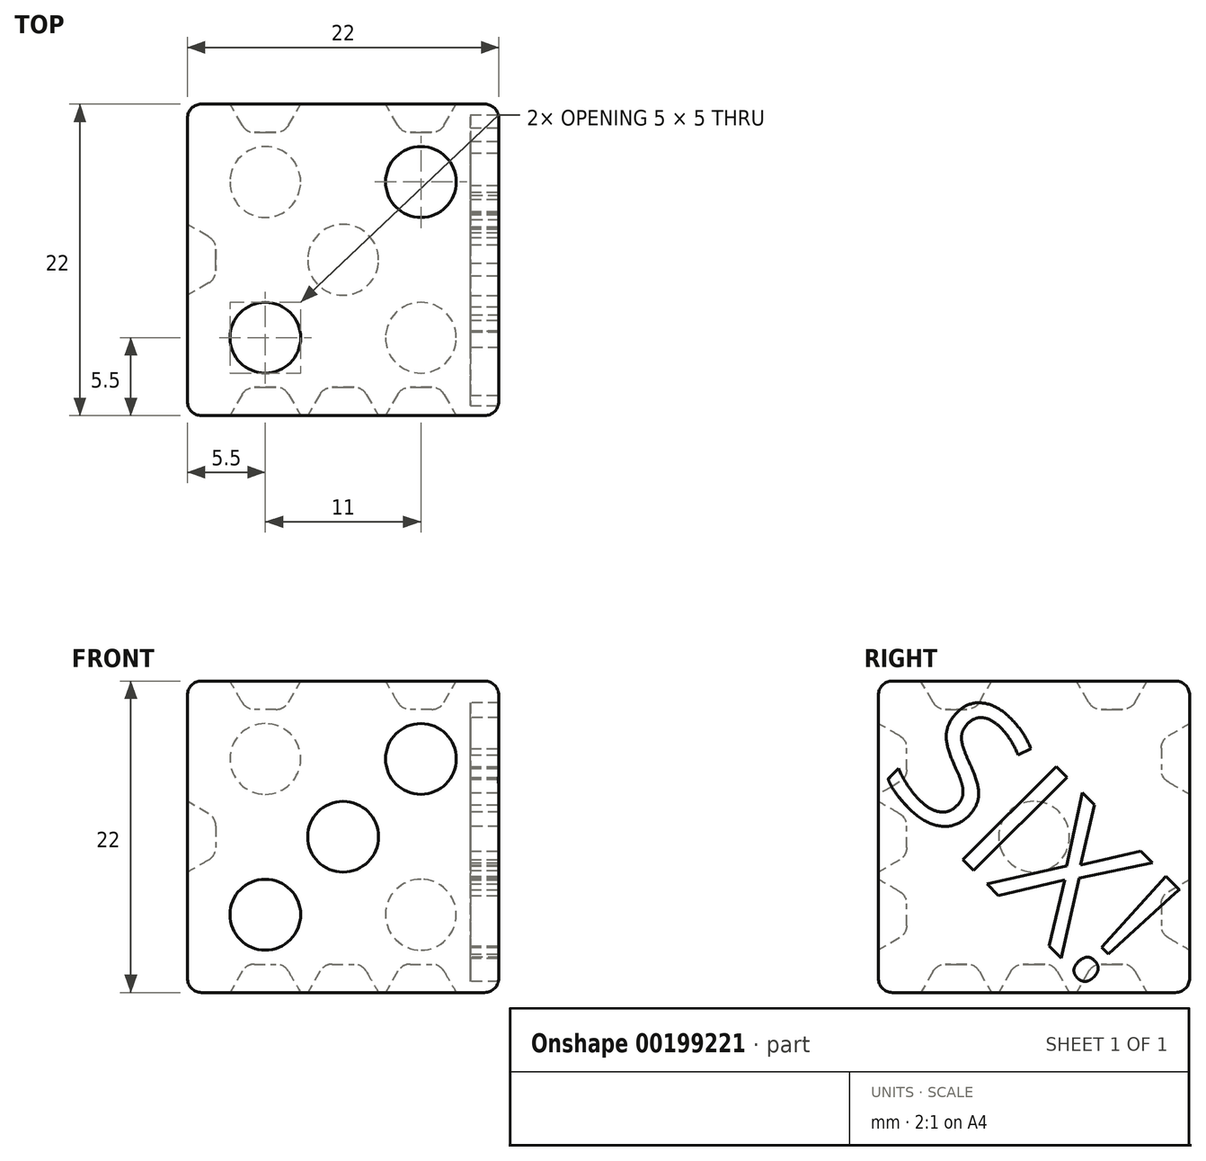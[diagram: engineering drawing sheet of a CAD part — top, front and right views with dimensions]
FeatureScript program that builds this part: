
annotation { "Feature Type Name" : "Feature", "Feature Type Description" : "" }
export const myFeature = defineFeature(function(context is Context, id is Id, definition is map)
    precondition{}
    {
        {
            var Q0;
            Q0=qCreatedBy(makeId("Top.planeOp"),FACE);
            var sketch = newSketch(context, id + "F0", { "sketchPlane" : qUnion([Q0])});
            skLineSegment(sketch, "E0.bottom", {"start": v(11, 11) * mm, "end": v(-11, 11) * mm});
            skLineSegment(sketch, "E0.top", {"start": v(11, -11) * mm, "end": v(-11, -11) * mm});
            skLineSegment(sketch, "E0.left", {"start": v(11, 11) * mm, "end": v(11, -11) * mm});
            skLineSegment(sketch, "E0.right", {"start": v(-11, 11) * mm, "end": v(-11, -11) * mm});
            skPoint(sketch, "E0.middle", {"position": v(0, 0) * mm});
            skSolve(sketch);
        }
        {
            var Q0;
            Q0=makeQuery(id+"F0.imprint","IMPRINT",FACE,{"disambiguationData":[TD([[makeQuery(id+"F0.imprint","IMPRINT",EDGE,{"derivedFrom":sQuery(id+"F0.wireOp",EDGE,"E0.bottom")}),1.0]])]});
            extrude(context, id + "F1", {"entities" : qUnion([Q0]), "depth" : 22 * mm});
        }
        {
            var Q0;
            Q0=makeQuery(id+"F1.opExtrude","SWEPT_FACE",FACE,{"disambiguationData":[OSD([sQuery(id+"F0.wireOp",EDGE,"E0.right")])]});
            var sketch = newSketch(context, id + "F2", { "sketchPlane" : qUnion([Q0])});
            skLineSegment(sketch, "E1", {"start": v(0, 22) * mm, "end": v(0, 0) * mm, "construction": true});
            skCircle(sketch, "E2", {"center": v(0, 11) * mm, "radius": 2.5 * mm});
            skSolve(sketch);
        }
        {
            var Q0;
            Q0 = qSketchRegion(id + "F2", true);
            extrude(context, id + "F3", {"entities" : qUnion([Q0]), "operationType" : NewBodyOperationType.REMOVE, "oppositeDirection" : true, "depth" : 2 * mm, "hasDraft" : true, "draftAngle" : 30 * degree, "draftPullDirection" : true});
        }
        {
            var Q0;
            Q0=makeQuery(id+"F1.opExtrude","CAP_FACE",FACE,{"disambiguationData":[OSD([sQuery(id+"F0.wireOp",EDGE,"E0.bottom"),sQuery(id+"F0.wireOp",EDGE,"E0.top"),sQuery(id+"F0.wireOp",EDGE,"E0.left"),sQuery(id+"F0.wireOp",EDGE,"E0.right")])],"isStart":false});
            var sketch = newSketch(context, id + "F4", { "sketchPlane" : qUnion([Q0])});
            skLineSegment(sketch, "E3", {"start": v(11, 11) * mm, "end": v(-11, -11) * mm, "construction": true});
            skLineSegment(sketch, "E4", {"start": v(11, 11) * mm, "end": v(11, 0) * mm, "construction": true});
            skLineSegment(sketch, "E5", {"start": v(11, 0) * mm, "end": v(-11, 0) * mm, "construction": true});
            skLineSegment(sketch, "E6", {"start": v(-11, 0) * mm, "end": v(-11, -11) * mm, "construction": true});
            skLineSegment(sketch, "E7", {"start": v(-11, -5.5) * mm, "end": v(11, -5.5) * mm, "construction": true});
            skLineSegment(sketch, "E8", {"start": v(11, 5.5) * mm, "end": v(-11, 5.5) * mm, "construction": true});
            skCircle(sketch, "E9", {"center": v(5.5, 5.5) * mm, "radius": 2.5 * mm});
            skCircle(sketch, "E10", {"center": v(-5.5, -5.5) * mm, "radius": 2.5 * mm});
            skSolve(sketch);
        }
        {
            var Q0;
            Q0 = qSketchRegion(id + "F4", true);
            extrude(context, id + "F5", {"entities" : qUnion([Q0]), "operationType" : NewBodyOperationType.REMOVE, "oppositeDirection" : true, "depth" : 2 * mm, "hasDraft" : true, "draftAngle" : 30 * degree, "draftPullDirection" : true});
        }
        {
            var Q0;
            Q0=makeQuery(id+"F1.opExtrude","SWEPT_FACE",FACE,{"disambiguationData":[OSD([sQuery(id+"F0.wireOp",EDGE,"E0.top")])]});
            var sketch = newSketch(context, id + "F6", { "sketchPlane" : qUnion([Q0])});
            skLineSegment(sketch, "E11", {"start": v(11, 11) * mm, "end": v(-11, 11) * mm, "construction": true});
            skLineSegment(sketch, "E12", {"start": v(11, 22) * mm, "end": v(0, 11) * mm, "construction": true});
            skLineSegment(sketch, "E13", {"start": v(0, 11) * mm, "end": v(-11, 0) * mm, "construction": true});
            skCircle(sketch, "E14", {"center": v(5.5, 16.5) * mm, "radius": 2.5 * mm});
            skCircle(sketch, "E15", {"center": v(0, 11) * mm, "radius": 2.5 * mm});
            skCircle(sketch, "E16", {"center": v(-5.5, 5.5) * mm, "radius": 2.5 * mm});
            skSolve(sketch);
        }
        {
            var Q0;
            Q0 = qSketchRegion(id + "F6", true);
            extrude(context, id + "F7", {"entities" : qUnion([Q0]), "operationType" : NewBodyOperationType.REMOVE, "oppositeDirection" : true, "depth" : 2 * mm, "hasDraft" : true, "draftAngle" : 30 * degree, "draftPullDirection" : true});
        }
        {
            var Q0;
            Q0=makeQuery(id+"F1.opExtrude","SWEPT_FACE",FACE,{"disambiguationData":[OSD([sQuery(id+"F0.wireOp",EDGE,"E0.bottom")])]});
            var sketch = newSketch(context, id + "F8", { "sketchPlane" : qUnion([Q0])});
            skLineSegment(sketch, "E17", {"start": v(-11, 22) * mm, "end": v(11, 22) * mm, "construction": true});
            skLineSegment(sketch, "E18", {"start": v(0, 22) * mm, "end": v(0, 11) * mm, "construction": true});
            skPoint(sketch, "E18.endSnap0", {"position": v(-11, 11) * mm});
            skLineSegment(sketch, "E19", {"start": v(0, 11) * mm, "end": v(0, 0) * mm, "construction": true});
            skLineSegment(sketch, "E20", {"start": v(0, 11) * mm, "end": v(11, 11) * mm, "construction": true});
            skLineSegment(sketch, "E21", {"start": v(0, 22) * mm, "end": v(11, 11) * mm, "construction": true});
            skCircle(sketch, "E22", {"center": v(5.5, 16.5) * mm, "radius": 2.5 * mm});
            skCircle(sketch, "E23.MirrorC", {"center": v(-5.5, 16.5) * mm, "radius": 2.5 * mm});
            skCircle(sketch, "E24.MirrorC", {"center": v(5.5, 5.5) * mm, "radius": 2.5 * mm});
            skCircle(sketch, "E25.MirrorC", {"center": v(-5.5, 5.5) * mm, "radius": 2.5 * mm});
            skSolve(sketch);
        }
        {
            var Q0;
            Q0 = qSketchRegion(id + "F8", true);
            extrude(context, id + "F9", {"entities" : qUnion([Q0]), "operationType" : NewBodyOperationType.REMOVE, "oppositeDirection" : true, "depth" : 2 * mm, "hasDraft" : true, "draftAngle" : 30 * degree, "draftPullDirection" : true});
        }
        {
            var Q0;
            Q0=makeQuery(id+"F1.opExtrude","CAP_FACE",FACE,{"disambiguationData":[OSD([sQuery(id+"F0.wireOp",EDGE,"E0.bottom"),sQuery(id+"F0.wireOp",EDGE,"E0.top"),sQuery(id+"F0.wireOp",EDGE,"E0.left"),sQuery(id+"F0.wireOp",EDGE,"E0.right")])],"isStart":true});
            var sketch = newSketch(context, id + "F10", { "sketchPlane" : qUnion([Q0])});
            skLineSegment(sketch, "E26", {"start": v(11, -11) * mm, "end": v(0, 0) * mm, "construction": true});
            skLineSegment(sketch, "E27", {"start": v(0, 0) * mm, "end": v(-11, 11) * mm, "construction": true});
            skLineSegment(sketch, "E28", {"start": v(11, 0) * mm, "end": v(-11, 0) * mm, "construction": true});
            skCircle(sketch, "E29", {"center": v(0, 0) * mm, "radius": 2.5 * mm});
            skCircle(sketch, "E30", {"center": v(5.5, -5.5) * mm, "radius": 2.5 * mm});
            skCircle(sketch, "E31", {"center": v(-5.5, 5.5) * mm, "radius": 2.5 * mm});
            skLineSegment(sketch, "E32", {"start": v(0, 0) * mm, "end": v(-11, -11) * mm, "construction": true});
            skLineSegment(sketch, "E33", {"start": v(0, 0) * mm, "end": v(11, 11) * mm, "construction": true});
            skCircle(sketch, "E34", {"center": v(5.5, 5.5) * mm, "radius": 2.5 * mm});
            skCircle(sketch, "E35", {"center": v(-5.5, -5.5) * mm, "radius": 2.5 * mm});
            skSolve(sketch);
        }
        {
            var Q0;
            Q0 = qSketchRegion(id + "F10", true);
            extrude(context, id + "F11", {"entities" : qUnion([Q0]), "operationType" : NewBodyOperationType.REMOVE, "oppositeDirection" : true, "depth" : 2 * mm, "hasDraft" : true, "draftAngle" : 30 * degree, "draftPullDirection" : true});
        }
        {
            var Q0;
            Q0=makeQuery(id+"F1.opExtrude","SWEPT_FACE",FACE,{"disambiguationData":[OSD([sQuery(id+"F0.wireOp",EDGE,"E0.left")])]});
            var sketch = newSketch(context, id + "F12", { "sketchPlane" : qUnion([Q0])});
            skText(sketch, "E36", { "text": "SIX!", "fontName": "OpenSans-Regular.ttf"});
            skLineSegment(sketch, "E37", {"start": v(11, 0) * mm, "end": v(-11, 22) * mm, "construction": true});
            skLineSegment(sketch, "E38", {"start": v(-11, 0) * mm, "end": v(0, 11) * mm, "construction": true});
            skPoint(sketch, "E38.endSnap0", {"position": v(0, 11) * mm});
            const initialGuessF12  = {"E36": [-0.011, 0.01535, 0.7071, -0.7071, 0.0094]};
            skSetInitialGuess(sketch, initialGuessF12);
            skSolve(sketch);
        }
        {
            var Q0;
            Q0 = qSketchRegion(id + "F12", true);
            extrude(context, id + "F13", {"entities" : qUnion([Q0]), "operationType" : NewBodyOperationType.REMOVE, "oppositeDirection" : true, "depth" : 2 * mm});
        }
        {
            var Q0;
            Q0=makeQuery(id+"F1.opExtrude","SWEPT_EDGE",EDGE,{"disambiguationData":[OSD([sQuery(id+"F0.wireOp",EDGE,"E0.top"),sQuery(id+"F0.wireOp",EDGE,"E0.left")])]});
            var Q1;
            Q1=makeQuery(id+"F1.opExtrude","CAP_EDGE",EDGE,{"disambiguationData":[OSD([sQuery(id+"F0.wireOp",EDGE,"E0.left")])],"isStart":true});
            var Q2;
            Q2=makeQuery(id+"F1.opExtrude","SWEPT_EDGE",EDGE,{"disambiguationData":[OSD([sQuery(id+"F0.wireOp",EDGE,"E0.bottom"),sQuery(id+"F0.wireOp",EDGE,"E0.left")])]});
            var Q3;
            Q3=makeQuery(id+"F1.opExtrude","CAP_EDGE",EDGE,{"disambiguationData":[OSD([sQuery(id+"F0.wireOp",EDGE,"E0.left")])],"isStart":false});
            var Q4;
            Q4=makeQuery(id+"F1.opExtrude","SWEPT_EDGE",EDGE,{"disambiguationData":[OSD([sQuery(id+"F0.wireOp",EDGE,"E0.top"),sQuery(id+"F0.wireOp",EDGE,"E0.right")])]});
            var Q5;
            Q5=makeQuery(id+"F1.opExtrude","CAP_EDGE",EDGE,{"disambiguationData":[OSD([sQuery(id+"F0.wireOp",EDGE,"E0.right")])],"isStart":true});
            var Q6;
            Q6=makeQuery(id+"F1.opExtrude","CAP_EDGE",EDGE,{"disambiguationData":[OSD([sQuery(id+"F0.wireOp",EDGE,"E0.top")])],"isStart":true});
            var Q7;
            Q7=makeQuery(id+"F1.opExtrude","CAP_EDGE",EDGE,{"disambiguationData":[OSD([sQuery(id+"F0.wireOp",EDGE,"E0.bottom")])],"isStart":true});
            var Q8;
            Q8=makeQuery(id+"F1.opExtrude","CAP_EDGE",EDGE,{"disambiguationData":[OSD([sQuery(id+"F0.wireOp",EDGE,"E0.top")])],"isStart":false});
            var Q9;
            Q9=makeQuery(id+"F1.opExtrude","SWEPT_EDGE",EDGE,{"disambiguationData":[OSD([sQuery(id+"F0.wireOp",EDGE,"E0.bottom"),sQuery(id+"F0.wireOp",EDGE,"E0.right")])]});
            var Q10;
            Q10=makeQuery(id+"F1.opExtrude","CAP_EDGE",EDGE,{"disambiguationData":[OSD([sQuery(id+"F0.wireOp",EDGE,"E0.bottom")])],"isStart":false});
            var Q11;
            Q11=makeQuery(id+"F1.opExtrude","CAP_EDGE",EDGE,{"disambiguationData":[OSD([sQuery(id+"F0.wireOp",EDGE,"E0.right")])],"isStart":false});
            var Q12;
            Q12=makeQuery(id+"F9.boolean.opBoolean","COPY",EDGE,{"derivedFrom":makeQuery(id+"F9.opExtrude","CAP_EDGE",EDGE,{"disambiguationData":[OSD([sQuery(id+"F8.wireOp",EDGE,"E22")])],"isStart":false})});
            var Q13;
            Q13=makeQuery(id+"F9.boolean.opBoolean","COPY",EDGE,{"derivedFrom":makeQuery(id+"F9.opExtrude","CAP_EDGE",EDGE,{"disambiguationData":[OSD([sQuery(id+"F8.wireOp",EDGE,"E24.MirrorC")])],"isStart":false})});
            var Q14;
            Q14=makeQuery(id+"F9.boolean.opBoolean","COPY",EDGE,{"derivedFrom":makeQuery(id+"F9.opExtrude","CAP_EDGE",EDGE,{"disambiguationData":[OSD([sQuery(id+"F8.wireOp",EDGE,"E25.MirrorC")])],"isStart":false})});
            var Q15;
            Q15=makeQuery(id+"F9.boolean.opBoolean","COPY",EDGE,{"derivedFrom":makeQuery(id+"F9.opExtrude","CAP_EDGE",EDGE,{"disambiguationData":[OSD([sQuery(id+"F8.wireOp",EDGE,"E23.MirrorC")])],"isStart":false})});
            var Q16;
            Q16=makeQuery(id+"F5.boolean.opBoolean","COPY",FACE,{"derivedFrom":makeQuery(id+"F5.opExtrude","CAP_FACE",FACE,{"disambiguationData":[OSD([sQuery(id+"F4.wireOp",EDGE,"E9")])],"isStart":false})});
            var Q17;
            Q17=makeQuery(id+"F5.boolean.opBoolean","COPY",EDGE,{"derivedFrom":makeQuery(id+"F5.opExtrude","CAP_EDGE",EDGE,{"disambiguationData":[OSD([sQuery(id+"F4.wireOp",EDGE,"E10")])],"isStart":false})});
            var Q18;
            Q18=makeQuery(id+"F11.boolean.opBoolean","COPY",FACE,{"derivedFrom":makeQuery(id+"F11.opExtrude","CAP_FACE",FACE,{"disambiguationData":[OSD([sQuery(id+"F10.wireOp",EDGE,"E35")])],"isStart":false})});
            var Q19;
            Q19=makeQuery(id+"F11.boolean.opBoolean","COPY",FACE,{"derivedFrom":makeQuery(id+"F11.opExtrude","CAP_FACE",FACE,{"disambiguationData":[OSD([sQuery(id+"F10.wireOp",EDGE,"E30")])],"isStart":false})});
            var Q20;
            Q20=makeQuery(id+"F11.boolean.opBoolean","COPY",FACE,{"derivedFrom":makeQuery(id+"F11.opExtrude","CAP_FACE",FACE,{"disambiguationData":[OSD([sQuery(id+"F10.wireOp",EDGE,"E29")])],"isStart":false})});
            var Q21;
            Q21=makeQuery(id+"F11.boolean.opBoolean","COPY",FACE,{"derivedFrom":makeQuery(id+"F11.opExtrude","CAP_FACE",FACE,{"disambiguationData":[OSD([sQuery(id+"F10.wireOp",EDGE,"E34")])],"isStart":false})});
            var Q22;
            Q22=makeQuery(id+"F11.boolean.opBoolean","COPY",FACE,{"derivedFrom":makeQuery(id+"F11.opExtrude","CAP_FACE",FACE,{"disambiguationData":[OSD([sQuery(id+"F10.wireOp",EDGE,"E31")])],"isStart":false})});
            var Q23;
            Q23=makeQuery(id+"F7.boolean.opBoolean","COPY",FACE,{"derivedFrom":makeQuery(id+"F7.opExtrude","CAP_FACE",FACE,{"disambiguationData":[OSD([sQuery(id+"F6.wireOp",EDGE,"E16")])],"isStart":false})});
            var Q24;
            Q24=makeQuery(id+"F7.boolean.opBoolean","COPY",EDGE,{"derivedFrom":makeQuery(id+"F7.opExtrude","CAP_EDGE",EDGE,{"disambiguationData":[OSD([sQuery(id+"F6.wireOp",EDGE,"E15")])],"isStart":false})});
            var Q25;
            Q25=makeQuery(id+"F3.boolean.opBoolean","COPY",EDGE,{"derivedFrom":makeQuery(id+"F3.opExtrude","CAP_EDGE",EDGE,{"disambiguationData":[OSD([sQuery(id+"F2.wireOp",EDGE,"E2")])],"isStart":false})});
            var Q26;
            Q26=makeQuery(id+"F7.boolean.opBoolean","COPY",EDGE,{"derivedFrom":makeQuery(id+"F7.opExtrude","CAP_EDGE",EDGE,{"disambiguationData":[OSD([sQuery(id+"F6.wireOp",EDGE,"E14")])],"isStart":false})});
            fillet(context, id + "F14", {"entities" : qUnion([Q0, Q1, Q2, Q3, Q4, Q5, Q6, Q7, Q8, Q9, Q10, Q11, Q12, Q13, Q14, Q15, Q16, Q17, Q18, Q19, Q20, Q21, Q22, Q23, Q24, Q25, Q26]), "radius" : 1 * mm, "tangentPropagation" : true, "allowEdgeOverflow" : false});
        }
    });
